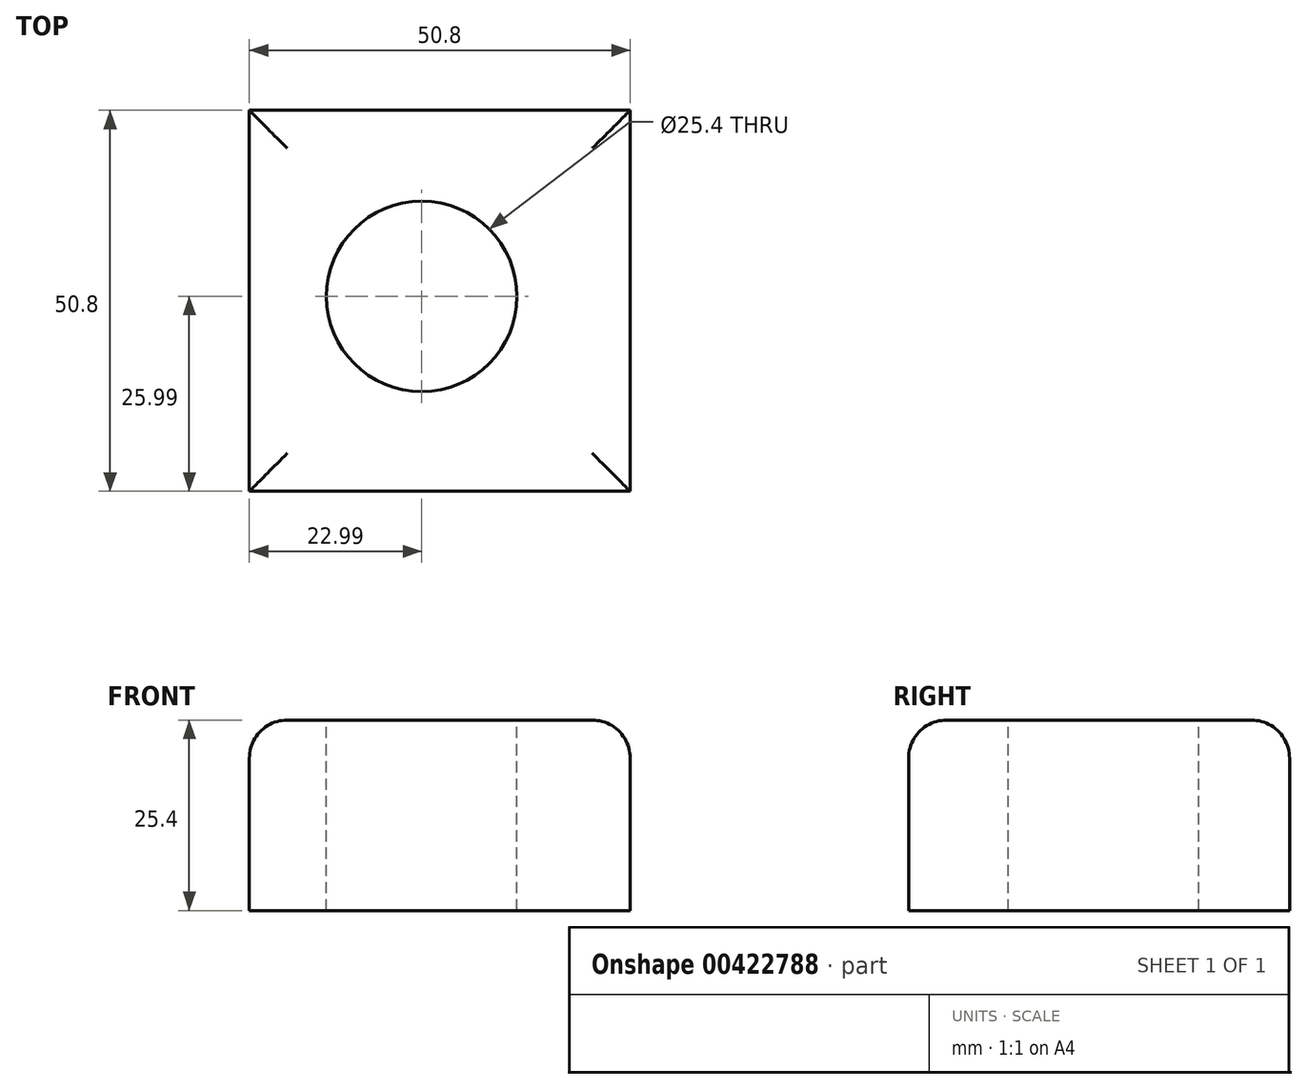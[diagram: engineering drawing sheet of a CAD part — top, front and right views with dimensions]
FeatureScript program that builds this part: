
annotation { "Feature Type Name" : "Feature", "Feature Type Description" : "" }
export const myFeature = defineFeature(function(context is Context, id is Id, definition is map)
    precondition{}
    {
        {
            var Q0;
            Q0=qCreatedBy(makeId("Top.planeOp"),FACE);
            var sketch = newSketch(context, id + "F0", { "sketchPlane" : qUnion([Q0])});
            skLineSegment(sketch, "E0.bottom", {"start": v(-23, 24.81) * mm, "end": v(27.8, 24.81) * mm});
            skLineSegment(sketch, "E0.top", {"start": v(-23, -25.99) * mm, "end": v(27.8, -25.99) * mm});
            skLineSegment(sketch, "E0.left", {"start": v(-23, 24.81) * mm, "end": v(-23, -25.99) * mm});
            skLineSegment(sketch, "E0.right", {"start": v(27.8, 24.81) * mm, "end": v(27.8, -25.99) * mm});
            skSolve(sketch);
        }
        {
            var Q0;
            Q0 = qSketchRegion(id + "F0", true);
            extrude(context, id + "F1", {"entities" : qUnion([Q0]), "depth" : 25.4 * mm});
        }
        {
            var Q0;
            Q0=makeQuery(id+"F1.opExtrude","CAP_FACE",FACE,{"disambiguationData":[OSD([sQuery(id+"F0.wireOp",EDGE,"E0.bottom"),sQuery(id+"F0.wireOp",EDGE,"E0.top"),sQuery(id+"F0.wireOp",EDGE,"E0.left"),sQuery(id+"F0.wireOp",EDGE,"E0.right")])],"isStart":false});
            var sketch = newSketch(context, id + "F2", { "sketchPlane" : qUnion([Q0])});
            skCircle(sketch, "E1", {"center": v(0, 0) * mm, "radius": 12.7 * mm});
            skSolve(sketch);
        }
        {
            var Q0;
            Q0 = qSketchRegion(id + "F2", true);
            extrude(context, id + "F3", {"entities" : qUnion([Q0]), "operationType" : NewBodyOperationType.REMOVE, "oppositeDirection" : true, "depth" : 25.4 * mm});
        }
        {
            var Q0;
            Q0=makeQuery(id+"F1.opExtrude","CAP_EDGE",EDGE,{"disambiguationData":[OSD([sQuery(id+"F0.wireOp",EDGE,"E0.top")])],"isStart":false});
            var Q1;
            Q1=makeQuery(id+"F1.opExtrude","CAP_EDGE",EDGE,{"disambiguationData":[OSD([sQuery(id+"F0.wireOp",EDGE,"E0.right")])],"isStart":false});
            var Q2;
            Q2=makeQuery(id+"F1.opExtrude","CAP_EDGE",EDGE,{"disambiguationData":[OSD([sQuery(id+"F0.wireOp",EDGE,"E0.bottom")])],"isStart":false});
            var Q3;
            Q3=makeQuery(id+"F1.opExtrude","CAP_EDGE",EDGE,{"disambiguationData":[OSD([sQuery(id+"F0.wireOp",EDGE,"E0.left")])],"isStart":false});
            fillet(context, id + "F4", {"entities" : qUnion([Q0, Q1, Q2, Q3]), "radius" : 5.08 * mm, "allowEdgeOverflow" : false});
        }
    });
